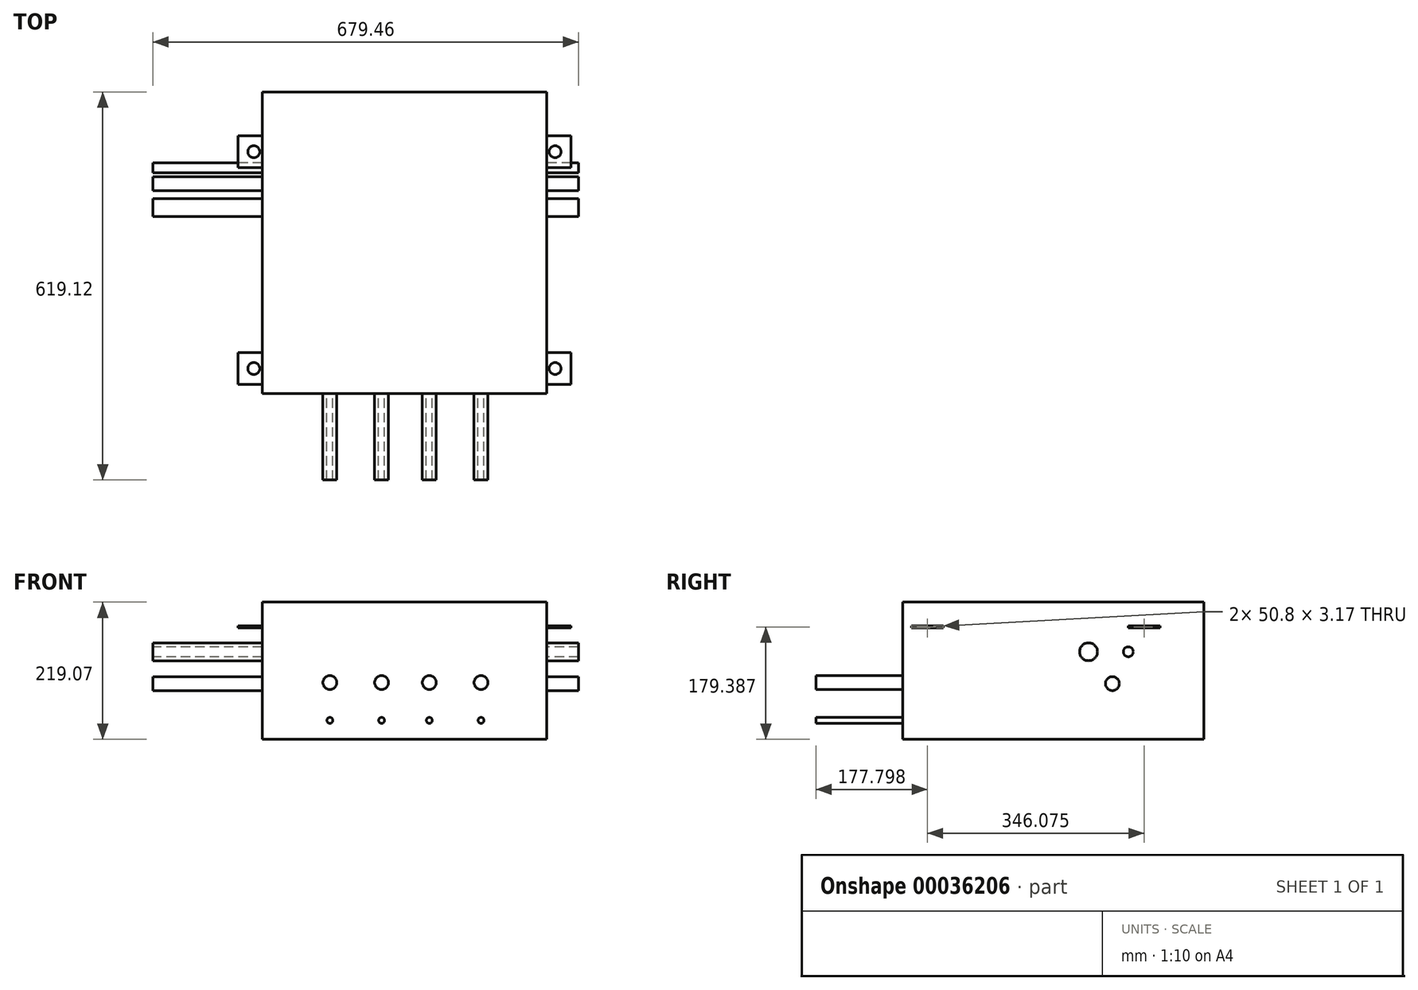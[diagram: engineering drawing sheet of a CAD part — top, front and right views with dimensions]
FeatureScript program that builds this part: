
annotation { "Feature Type Name" : "Feature", "Feature Type Description" : "" }
export const myFeature = defineFeature(function(context is Context, id is Id, definition is map)
    precondition{}
    {
        {
            var Q0;
            Q0=qCreatedBy(makeId("Front.planeOp"),FACE);
            var sketch = newSketch(context, id + "F0", { "sketchPlane" : qUnion([Q0])});
            skLineSegment(sketch, "E0.bottom", {"start": v(0, 0) * mm, "end": v(454.03, 0) * mm});
            skLineSegment(sketch, "E0.top", {"start": v(0, 219.07) * mm, "end": v(454.03, 219.07) * mm});
            skLineSegment(sketch, "E0.left", {"start": v(0, 0) * mm, "end": v(0, 219.07) * mm});
            skLineSegment(sketch, "E0.right", {"start": v(454.03, 0) * mm, "end": v(454.03, 219.08) * mm});
            skSolve(sketch);
        }
        {
            var Q0;
            Q0=qSketchRegion(id+"F0",true);
            extrude(context, id + "F1", {"entities" : qUnion([Q0]), "oppositeDirection" : true, "depth" : 481 * mm});
        }
        {
            var Q0;
            Q0=qCreatedBy(makeId("Front.planeOp"),FACE);
            var sketch = newSketch(context, id + "F2", { "sketchPlane" : qUnion([Q0])});
            skLineSegment(sketch, "E1.bottom", {"start": v(107.95, 90.49) * mm, "end": v(349.25, 90.49) * mm, "construction": true});
            skLineSegment(sketch, "E1.top", {"start": v(107.95, 30.16) * mm, "end": v(349.25, 30.16) * mm, "construction": true});
            skLineSegment(sketch, "E1.left", {"start": v(107.95, 90.49) * mm, "end": v(107.95, 30.16) * mm, "construction": true});
            skLineSegment(sketch, "E1.right", {"start": v(349.25, 90.49) * mm, "end": v(349.25, 30.16) * mm, "construction": true});
            skCircle(sketch, "E2", {"center": v(107.95, 90.49) * mm, "radius": 11.11 * mm});
            skCircle(sketch, "E3", {"center": v(107.95, 30.16) * mm, "radius": 4.76 * mm});
            skCircle(sketch, "E4", {"center": v(349.25, 90.49) * mm, "radius": 11.11 * mm});
            skCircle(sketch, "E5", {"center": v(349.25, 30.16) * mm, "radius": 4.76 * mm});
            skCircle(sketch, "E6", {"center": v(190.5, 90.49) * mm, "radius": 11.11 * mm});
            skCircle(sketch, "E7", {"center": v(266.7, 90.49) * mm, "radius": 11.11 * mm});
            skCircle(sketch, "E8", {"center": v(190.5, 30.16) * mm, "radius": 4.76 * mm});
            skCircle(sketch, "E9", {"center": v(266.7, 30.16) * mm, "radius": 4.76 * mm});
            skLineSegment(sketch, "E10", {"start": v(190.5, 30.16) * mm, "end": v(190.5, 90.49) * mm, "construction": true});
            skLineSegment(sketch, "E11", {"start": v(266.7, 30.16) * mm, "end": v(266.7, 90.49) * mm, "construction": true});
            skSolve(sketch);
        }
        {
            var Q0;
            Q0=qSketchRegion(id+"F2",true);
            extrude(context, id + "F3", {"entities" : qUnion([Q0]), "operationType" : NewBodyOperationType.ADD, "depth" : 138.11 * mm});
        }
        {
            var Q0;
            Q0=makeQuery(id+"F1.opExtrude","SWEPT_FACE",FACE,{"disambiguationData":[OSD([sQuery(id+"F0.wireOp",EDGE,"E0.right")])]});
            var sketch = newSketch(context, id + "F4", { "sketchPlane" : qUnion([Q0])});
            skCircle(sketch, "E12", {"center": v(296.86, 139.7) * mm, "radius": 14.29 * mm});
            skCircle(sketch, "E13", {"center": v(360.36, 139.7) * mm, "radius": 7.94 * mm});
            skCircle(sketch, "E14", {"center": v(334.96, 88.9) * mm, "radius": 11.11 * mm});
            skSolve(sketch);
        }
        {
            var Q0;
            Q0=qSketchRegion(id+"F4",true);
            extrude(context, id + "F5", {"entities" : qUnion([Q0]), "operationType" : NewBodyOperationType.ADD, "depth" : 174.62 * mm, "hasSecondDirection" : true, "secondDirectionOppositeDirection" : true, "secondDirectionDepth" : 628.65 * mm});
        }
        {
            var Q0;
            Q0=makeQuery(id+"F1.opExtrude","SWEPT_FACE",FACE,{"disambiguationData":[OSD([sQuery(id+"F0.wireOp",EDGE,"E0.top")])]});
            cPlane(context, id + "F6", {"entities" : qUnion([Q0]), "cplaneType" : CPlaneType.OFFSET, "offset" : 38.1 * mm, "oppositeDirection" : true, "width" : 152.4 * mm, "height" : 152.4 * mm});
        }
        {
            var Q0;
            Q0=qCreatedBy(id+"F6.planeOp",FACE);
            var sketch = newSketch(context, id + "F7", { "sketchPlane" : qUnion([Q0])});
            skLineSegment(sketch, "E15.bottom", {"start": v(-38.9, 411.16) * mm, "end": v(0, 411.16) * mm});
            skLineSegment(sketch, "E15.top", {"start": v(-38.9, 360.36) * mm, "end": v(0, 360.36) * mm});
            skLineSegment(sketch, "E15.left", {"start": v(-38.9, 411.16) * mm, "end": v(-38.9, 360.36) * mm});
            skLineSegment(sketch, "E15.right", {"start": v(0, 411.16) * mm, "end": v(0, 360.36) * mm});
            skLineSegment(sketch, "E16.bottom", {"start": v(-38.9, 65.09) * mm, "end": v(0, 65.09) * mm});
            skLineSegment(sketch, "E16.top", {"start": v(-38.9, 14.29) * mm, "end": v(0, 14.29) * mm});
            skLineSegment(sketch, "E16.left", {"start": v(-38.9, 65.09) * mm, "end": v(-38.9, 14.29) * mm});
            skLineSegment(sketch, "E16.right", {"start": v(0, 65.09) * mm, "end": v(0, 14.29) * mm});
            skLineSegment(sketch, "E17.bottom", {"start": v(454.03, 411.16) * mm, "end": v(492.92, 411.16) * mm});
            skLineSegment(sketch, "E17.top", {"start": v(454.03, 360.36) * mm, "end": v(492.92, 360.36) * mm});
            skLineSegment(sketch, "E17.left", {"start": v(454.03, 411.16) * mm, "end": v(454.03, 360.36) * mm});
            skLineSegment(sketch, "E17.right", {"start": v(492.92, 411.16) * mm, "end": v(492.92, 360.36) * mm});
            skLineSegment(sketch, "E18.bottom", {"start": v(454.03, 65.09) * mm, "end": v(492.92, 65.09) * mm});
            skLineSegment(sketch, "E18.top", {"start": v(454.03, 14.29) * mm, "end": v(492.92, 14.29) * mm});
            skLineSegment(sketch, "E18.left", {"start": v(454.03, 65.09) * mm, "end": v(454.03, 14.29) * mm});
            skLineSegment(sketch, "E18.right", {"start": v(492.92, 65.09) * mm, "end": v(492.92, 14.29) * mm});
            skLineSegment(sketch, "E19", {"start": v(-38.9, 385.76) * mm, "end": v(-13.5, 385.76) * mm, "construction": true});
            skLineSegment(sketch, "E20", {"start": v(-38.9, 39.69) * mm, "end": v(-13.5, 39.69) * mm, "construction": true});
            skLineSegment(sketch, "E21", {"start": v(492.92, 39.69) * mm, "end": v(467.52, 39.69) * mm, "construction": true});
            skLineSegment(sketch, "E22", {"start": v(492.92, 385.76) * mm, "end": v(467.52, 385.76) * mm, "construction": true});
            skPoint(sketch, "E22.endSnap0", {"position": v(492.92, 385.76) * mm});
            skCircle(sketch, "E23", {"center": v(-13.5, 39.69) * mm, "radius": 9.53 * mm});
            skCircle(sketch, "E24", {"center": v(-13.5, 385.76) * mm, "radius": 9.53 * mm});
            skCircle(sketch, "E25", {"center": v(467.52, 385.76) * mm, "radius": 9.53 * mm});
            skCircle(sketch, "E26", {"center": v(467.52, 39.69) * mm, "radius": 9.53 * mm});
            skSolve(sketch);
        }
        {
            var Q0;
            Q0=qSketchRegion(id+"F7",true);
            extrude(context, id + "F8", {"entities" : qUnion([Q0]), "operationType" : NewBodyOperationType.ADD, "oppositeDirection" : true, "depth" : 3.17 * mm});
        }
        {
            var Q0;
            Q0=makeQuery(id+"F1.opExtrude","CAP_FACE",FACE,{"disambiguationData":[OSD([sQuery(id+"F0.wireOp",EDGE,"E0.bottom"),sQuery(id+"F0.wireOp",EDGE,"E0.top"),sQuery(id+"F0.wireOp",EDGE,"E0.left"),sQuery(id+"F0.wireOp",EDGE,"E0.right")])],"isStart":true});
            var sketch = newSketch(context, id + "F9", { "sketchPlane" : qUnion([Q0])});
            skLineSegment(sketch, "E27.bottom", {"start": v(504.82, 219.08) * mm, "end": v(657.22, 219.08) * mm});
            skLineSegment(sketch, "E27.top", {"start": v(504.82, 0) * mm, "end": v(657.22, 0) * mm});
            skLineSegment(sketch, "E27.left", {"start": v(504.82, 219.08) * mm, "end": v(504.82, 0) * mm});
            skLineSegment(sketch, "E27.right", {"start": v(657.22, 219.08) * mm, "end": v(657.22, 0) * mm});
            skSolve(sketch);
        }
        {
            var Q0;
            Q0 = qSketchRegion(id + "F9", true);
            extrude(context, id + "F10", {"entities" : qUnion([Q0]), "operationType" : NewBodyOperationType.REMOVE, "endBound" : BoundingType.THROUGH_ALL, "oppositeDirection" : true, "depth" : 25.4 * mm});
        }
    });
